# Revit family: axor_flowstar_design_trap_51303000
name_source: partatom
category: Plumbing Fixtures
revit_build: Autodesk Revit 2015 (Build: 20140903_1530(x64)
units: mm (PartAtom-declared; Revit-internal decimal feet)

## types (1)
- Chrome 000
    BIMobject category = Pipes
    BOSUseNativeGeometries = 1
    Default Elevation = 4' - 0"
    Design country = Germany
    EAN code = https://4059625077795
    Edition number = 1
    IFC Classification = Sanitary Terminal
    Installation instructions = https://pro.hansgrohe-int.com
    Manufacturer country = Germany
    Manufacturer name = AXOR
    Masterformat 2014 Code = 22 00 00
    Masterformat 2014 Description = Plumbing
    Material main = Chrome
    NBS Reference Code = 62-64
    NBS Reference Description = Pipe Fittings
    Nominal height = 0
    Nominal width = 0
    OmniClass Code = 23-31 35 00
    OmniClass Description = Plumbing Tubing
    Product Guid = dc509fda-0b00-4bf1-bcf7-61f90ed825ff
    Product SKU = 51303000
    Product data url = https://bimobject.com
    Product family = Wastes and overflows
    Product group = Traps
    Product name = AXOR Flowstar design trap 51303000
    Product url = https://pro.hansgrohe-int.com
    QR code = http://bimobject.com
    Technical description = https://pro.hansgrohe-int.com
    UNSPSC Code = 3018
    Uniclass 1.4 Code = L73121
    Uniclass 1.4 Description = Pipes and fittings
    Uniclass 2.0 Code = PR-62-64
    Uniclass 2.0 Description = Pipe Fittings
    Uniclass 2015 Code = Pr_60_45_90
    Uniclass 2015 Name = Wastewater and water mixer products
    Uniformat II Code = D2010
    Uniformat II Description = Plumbing Fixtures
    Weight Net (Kg) = 0

## geometry (parser evidence)
native form markers: Sweep x2
no freeform markers — native parametric forms only
